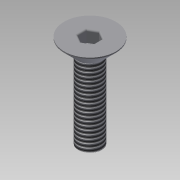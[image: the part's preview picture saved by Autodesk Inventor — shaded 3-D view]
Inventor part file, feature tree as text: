
AUTODESK INVENTOR PART (.ipt)
format: ipt  version: 2014 (Build 180170000, 170)  size: 128,512 bytes
history: native  units: mm
features: extrude x4, sketch x4, thread x1, fillet x1
ambient origin geometry x8: Origin, YZ Plane, XZ Plane, XY Plane, X Axis, Y Axis, Z Axis, Center Point
bodies: Solid1 (feature_tree)
feature tree (10):
  extrude  "Extrusion1"  Depth=5.0mm TaperAngle=0.0deg
  extrude  "Extrusion2"  Depth=2.0mm
  extrude  "Extrusion3"  Depth=10.0mm TaperAngle=0.0deg
  thread  "Thread1"  [1 undecoded]
  extrude  "Extrusion4"  Depth=0.2mm
  fillet  "Fillet1"  [1 undecoded]
  sketch  "Sketch1"  dims[d0=3.0mm d1=5.0mm d2=0.0mm]
  sketch  "Sketch2"  dims[d3=2.0mm d4=45.0deg d5=6.7mm]
  sketch  "Sketch3"  dims[d6=2.0mm d7=0.0mm d8=10.0mm d9=0.0mm d10=1.0mm]
  sketch  "Sketch4"  dims[d11=1.5mm d12=0.0mm d13=0.2mm]
note: 2 required parameter values undecoded (feature->parameter linkage not recoverable at this tier; creation-order binding heuristic only, values carry confidence <= 0.55)
